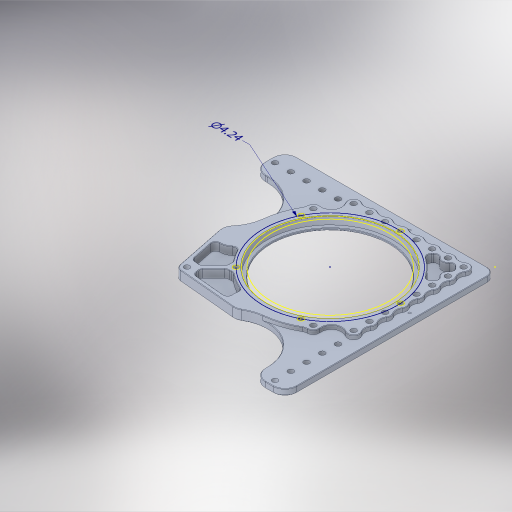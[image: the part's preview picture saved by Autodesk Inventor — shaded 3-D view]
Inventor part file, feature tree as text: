
AUTODESK INVENTOR PART (.ipt)
format: ipt  version: 2023.4 (Build 274418000, 418)  size: 582,656 bytes
history: native  units: in
note: dims shown in document units (in); Inventor stores cm internally (conversion verified against a paired STEP export)
features: other x3, sketch x1
ambient origin geometry x8: Origin, YZ Plane, XZ Plane, XY Plane, X Axis, Y Axis, Z Axis, Center Point
bodies: Solid1 (feature_tree)
feature tree (4):
  other  "Annotations"
  sketch  "Sketch1"  dims[d0=1.0702in d1=4.24in]
  other  "MK4i Master Part V2_NEO Config"
  other  "Diameter Dimension 1"
